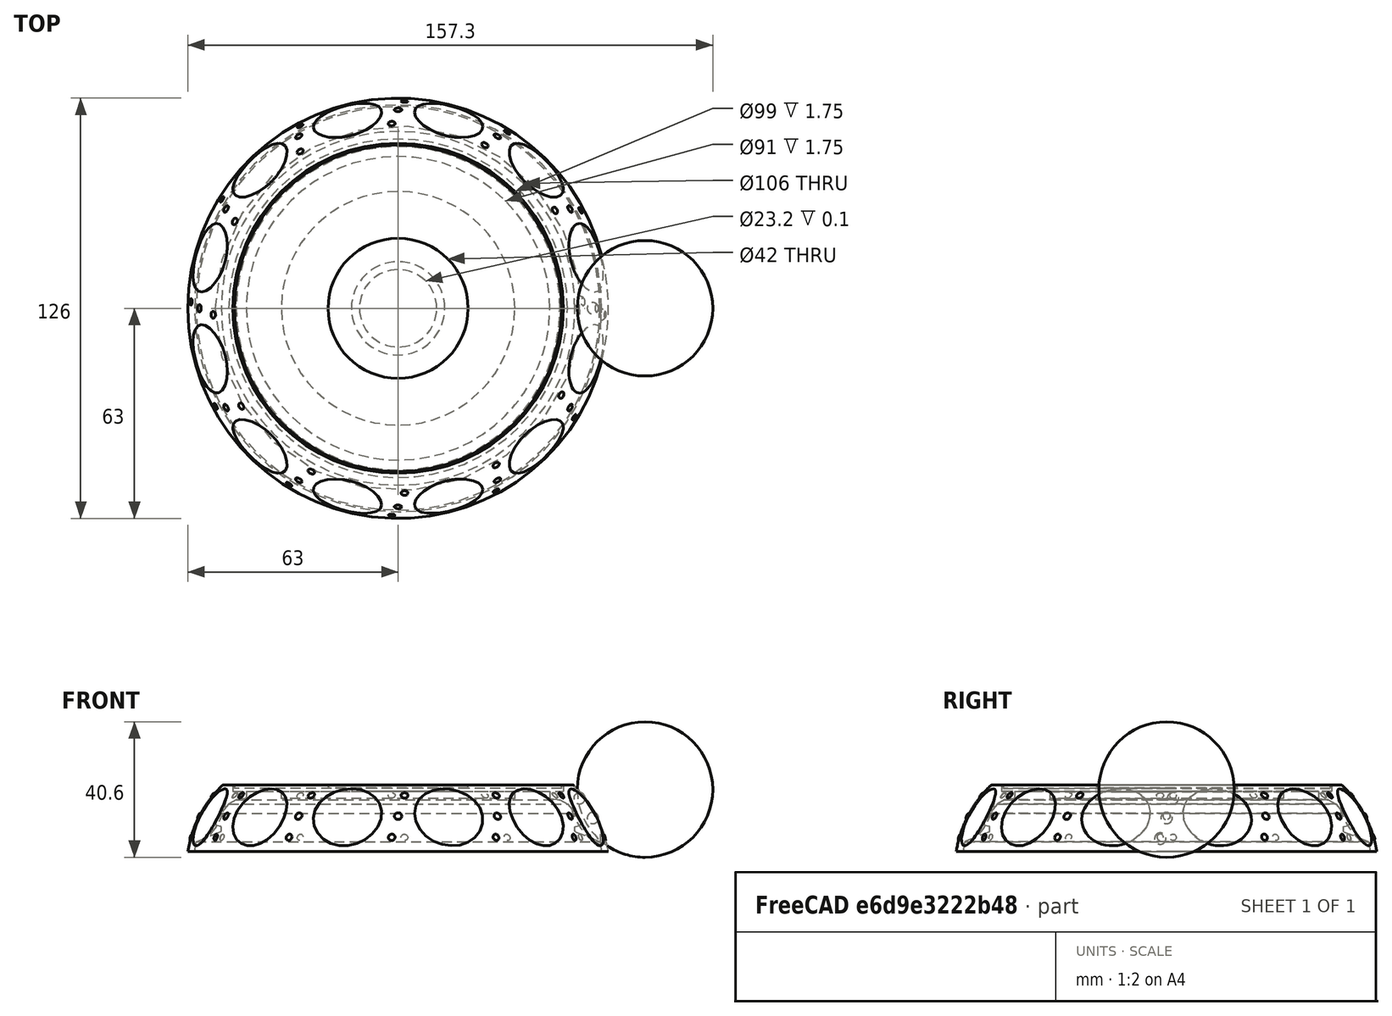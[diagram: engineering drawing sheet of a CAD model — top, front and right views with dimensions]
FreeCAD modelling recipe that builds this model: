
FCSTD DOCUMENT  (FreeCAD 0.20R29177 (Git))
Label: Jog
License: All rights reserved
LicenseURL: http://en.wikipedia.org/wiki/All_rights_reserved
objects: Part::Cylinder×6, Part::Sphere×4, Part::FeaturePython×4, Part::Cut×3, Part::Fuse×3, Sketcher::SketchObject×1, Part::Revolution×1
note: 18 computed .brp shape members not serialized (recipe doc carries the construction recipe); baked Part::Feature solids carry a one-line shape summary decoded from their .brp

FEATURE [Part::Cylinder] Cylinder  label="Поверхность джога"
  Angle = 360
  AttacherType = Attacher::AttachEngine3D
  FirstAngle = 0
  Height = 1
  Placement = pos=(0,0,19) rot=(0,0,1;0rad)
  Radius = 49
  SecondAngle = 0
FEATURE [Sketcher::SketchObject] Sketch
  FullyConstrained = false
  Placement = pos=(0,0,0) rot=(1,0,0;1.5708rad)
  sketch-geometry (20):
    g0: ArcOfCircle CenterX=-28.5028 CenterY=-5.35479 CenterZ=0 NormalX=0 NormalY=0 NormalZ=1 AngleXU=0 Radius=34.9103 StartAngle=2.33675 EndAngle=2.9876
    g1: LineSegment StartX=-61 StartY=0 StartZ=0 EndX=-60.5 EndY=3 EndZ=0
    g2: LineSegment StartX=-54.6347 StartY=8.63919 StartZ=0 EndX=-53 EndY=11.5 EndZ=0
    g3: LineSegment StartX=-63 StartY=0 StartZ=0 EndX=-61 EndY=0 EndZ=0
    g4: LineSegment StartX=-52.2215 StartY=20 StartZ=0 EndX=-49.75 EndY=20 EndZ=0
    g5: LineSegment StartX=-49.5 StartY=19.75 StartZ=0 EndX=-49.5 EndY=18 EndZ=0
    g6: LineSegment StartX=-49.5 StartY=18 StartZ=0 EndX=-45.5 EndY=18 EndZ=0
    g7: LineSegment StartX=-45.7466 StartY=15.9589 StartZ=0 EndX=-48.5 EndY=15.5 EndZ=0
    g8: LineSegment StartX=-48.5 StartY=15.5 StartZ=0 EndX=-50.75 EndY=14.25 EndZ=0
    g9: LineSegment StartX=-50.75 StartY=14.25 StartZ=0 EndX=-53 EndY=11.5 EndZ=0
    g10: LineSegment StartX=-60.5 StartY=3 StartZ=0 EndX=-53.1682 EndY=5.93271 EndZ=0
    g11: LineSegment StartX=-45.5 StartY=18 StartZ=0 EndX=-45.5 EndY=16.25 EndZ=0
    g12: ArcOfCircle CenterX=-52.2215 CenterY=19.3046 CenterZ=0 NormalX=0 NormalY=0 NormalZ=1 AngleXU=0 Radius=0.695441 StartAngle=1.5708 EndAngle=2.33675
    g13: ArcOfCircle CenterX=-45.7951 CenterY=16.25 CenterZ=0 NormalX=0 NormalY=0 NormalZ=1 AngleXU=0 Radius=0.295115 StartAngle=4.87754 EndAngle=6.28319
    g14: ArcOfCircle CenterX=-49.75 CenterY=19.75 CenterZ=0 NormalX=0 NormalY=0 NormalZ=1 AngleXU=0 Radius=0.25 StartAngle=0 EndAngle=1.5708
    g15: LineSegment StartX=-53 StartY=6.18117 StartZ=0 EndX=-53 EndY=7.27425 EndZ=0
    g16: LineSegment StartX=-53.219 StartY=7.55475 StartZ=0 EndX=-54.2858 EndY=7.82145 EndZ=0
    g17: ArcOfCircle CenterX=-54.1505 CenterY=8.3625 CenterZ=0 NormalX=0 NormalY=0 NormalZ=1 AngleXU=0 Radius=0.5577 StartAngle=2.62245 EndAngle=4.46741
    g18: ArcOfCircle CenterX=-53.2891 CenterY=7.27425 CenterZ=0 NormalX=0 NormalY=0 NormalZ=1 AngleXU=0 Radius=0.289138 StartAngle=2e-16 EndAngle=1.32582
    g19: ArcOfCircle CenterX=-53.2676 CenterY=6.18117 CenterZ=0 NormalX=0 NormalY=0 NormalZ=1 AngleXU=0 Radius=0.267599 StartAngle=5.0929 EndAngle=6.28319
  constraints (16):
    c: DistanceX(g0) = -63
    c: DistanceY(g0) = 0
    c: DistanceX(g1) = -61
    c: DistanceY(g1) = 0
    c: Tangent(g0,g12) = -1.5708
    c: Tangent(g4,g12) = 1.5708
    c: Tangent(g11,g13) = 1.5708
    c: Tangent(g7,g13) = 1.5708
    c: Tangent(g4,g14) = 1.5708
    c: Tangent(g5,g14) = 1.5708
    c: Tangent(g2,g17) = 1.5708
    c: Tangent(g16,g17) = 1.5708
    c: Tangent(g16,g18) = -1.5708
    c: Tangent(g15,g18) = -1.5708
    c: Tangent(g10,g19) = -1.5708
    c: Tangent(g15,g19) = -1.5708
FEATURE [Part::Revolution] Revolve
  Angle = 360
  Axis = (0,0,1)
  Base = (0,0,0)
  FaceMakerClass = Part::FaceMakerBullseye
  Solid = true
  Source = -> Sketch
  Symmetric = false
FEATURE [Part::Sphere] Sphere  label="Сфера"
  Angle1 = -90
  Angle2 = 90
  Angle3 = 360
  AttacherType = Attacher::AttachEngine3D
  Placement = pos=(74,0,18.6) rot=(0,0,1;0rad)
  Radius = 20.3
FEATURE [Part::FeaturePython] Array  # Draft array (typed FeaturePython)
  AlwaysSyncPlacement = false
  Angle = 360
  ArrayType = 1
  Axis = (0,0,1)
  Base = -> Sphere
  Center = (0,0,18.6)
  Count = 12
  ExpandArray = false
  Fuse = false
  IntervalAxis = (0,0,0)
  IntervalX = (50,0,0)
  IntervalY = (0,50,0)
  IntervalZ = (0,0,50)
  NumberCircles = 3
  NumberPolar = 12
  NumberX = 2
  NumberY = 2
  NumberZ = 1
  Placement = pos=(0,0,0) rot=(0,0,1;0.261799rad)
  PlacementList = 12 placements: [(74,0,18.6),(64.0859,37,18.6),(37,64.0859,18.6),(0,74,18.6),(-37,64.0859,18.6),(-64.0859,37,18.6),(-74,9.06239e-15,18.6),(-64.0859,-37,18.6),(-37,-64.0859,18.6),(-1.42109e-14,-74,18.6),(37,-64.0859,18.6),(64.0859,-37,18.6)]
  RadialDistance = 50
  ScaleList = (12) [(1,1,1),(1,1,1),(1,1,1),(1,1,1),(1,1,1),(1,1,1),(1,1,1),(1,1,1),(1,1,1),(1,1,1),(1,1,1),(1,1,1)]
  Symmetry = 1
  TangentialDistance = 25
FEATURE [Part::Cut] Cut
  Base = -> Revolve
  Tool = -> Array
FEATURE [Part::Sphere] Sphere001  label="Сфера центральная"
  Angle1 = -90
  Angle2 = 90
  Angle3 = 360
  AttacherType = Attacher::AttachEngine3D
  Placement = pos=(58.38,0,10.05) rot=(0,0,-1;1.5708rad)
  Radius = 1.7
FEATURE [Part::Sphere] Sphere002  label="Сфера нижняя"
  Angle1 = -90
  Angle2 = 90
  Angle3 = 180
  AttacherType = Attacher::AttachEngine3D
  Placement = pos=(60.69,-1.87,3.9) rot=(0,0,-1;1.5708rad)
  Radius = 1.7
FEATURE [Part::Sphere] Sphere003  label="Сфера верхняя"
  Angle1 = -90
  Angle2 = 90
  Angle3 = 360
  AttacherType = Attacher::AttachEngine3D
  Placement = pos=(54.36,1.9,16) rot=(0,0,-1;1.5708rad)
  Radius = 1.7
FEATURE [Part::FeaturePython] Array001  # Draft array (typed FeaturePython)
  AlwaysSyncPlacement = false
  Angle = 360
  ArrayType = 1
  Axis = (0,0,1)
  Base = -> Sphere001
  Center = (0,0,10.05)
  Count = 12
  ExpandArray = false
  Fuse = false
  IntervalAxis = (0,0,0)
  IntervalX = (50,0,0)
  IntervalY = (0,50,0)
  IntervalZ = (0,0,50)
  NumberCircles = 3
  NumberPolar = 12
  NumberX = 2
  NumberY = 2
  NumberZ = 1
  PlacementList = 12 placements: [(58.38,0,10.05),(50.5586,29.19,10.05),(29.19,50.5586,10.05),(0,58.38,10.05),(-29.19,50.5586,10.05),(-50.5586,29.19,10.05),(-58.38,7.14949e-15,10.05),(-50.5586,-29.19,10.05),(-29.19,-50.5586,10.05),(-1.42109e-14,-58.38,10.05),(29.19,-50.5586,10.05),(50.5586,-29.19,10.05)]
  RadialDistance = 50
  ScaleList = (12) [(1,1,1),(1,1,1),(1,1,1),(1,1,1),(1,1,1),(1,1,1),(1,1,1),(1,1,1),(1,1,1),(1,1,1),(1,1,1),(1,1,1)]
  Symmetry = 1
  TangentialDistance = 25
FEATURE [Part::FeaturePython] Array002  # Draft array (typed FeaturePython)
  AlwaysSyncPlacement = false
  Angle = 360
  ArrayType = 1
  Axis = (0,0,1)
  Base = -> Sphere002
  Center = (0,0,3.9)
  Count = 12
  ExpandArray = false
  Fuse = false
  IntervalAxis = (0,0,0)
  IntervalX = (50,0,0)
  IntervalY = (0,50,0)
  IntervalZ = (0,0,50)
  NumberCircles = 3
  NumberPolar = 12
  NumberX = 2
  NumberY = 2
  NumberZ = 1
  PlacementList = 12 placements: [(60.69,-1.87,3.9),(53.4941,28.7255,3.9),(31.9645,51.6241,3.9),(1.87,60.69,3.9),(-28.7255,53.4941,3.9),(-51.6241,31.9645,3.9),(-60.69,1.87,3.9),(-53.4941,-28.7255,3.9),(-31.9645,-51.6241,3.9),(-1.87,-60.69,3.9),(28.7255,-53.4941,3.9),(51.6241,-31.9645,3.9)]
  RadialDistance = 50
  ScaleList = (12) [(1,1,1),(1,1,1),(1,1,1),(1,1,1),(1,1,1),(1,1,1),(1,1,1),(1,1,1),(1,1,1),(1,1,1),(1,1,1),(1,1,1)]
  Symmetry = 1
  TangentialDistance = 25
FEATURE [Part::FeaturePython] Array003  # Draft array (typed FeaturePython)
  AlwaysSyncPlacement = false
  Angle = 360
  ArrayType = 1
  Axis = (0,0,1)
  Base = -> Sphere003
  Center = (0,0,16)
  Count = 12
  ExpandArray = false
  Fuse = false
  IntervalAxis = (0,0,0)
  IntervalX = (50,0,0)
  IntervalY = (0,50,0)
  IntervalZ = (0,0,50)
  NumberCircles = 3
  NumberPolar = 12
  NumberX = 2
  NumberY = 2
  NumberZ = 1
  PlacementList = 12 placements: [(54.36,1.9,16),(46.1271,28.8254,16),(25.5346,48.0271,16),(-1.9,54.36,16),(-28.8254,46.1271,16),(-48.0271,25.5346,16),(-54.36,-1.9,16),(-46.1271,-28.8254,16),(-25.5346,-48.0271,16),(1.9,-54.36,16),(28.8254,-46.1271,16),(48.0271,-25.5346,16)]
  RadialDistance = 50
  ScaleList = (12) [(1,1,1),(1,1,1),(1,1,1),(1,1,1),(1,1,1),(1,1,1),(1,1,1),(1,1,1),(1,1,1),(1,1,1),(1,1,1),(1,1,1)]
  Symmetry = 1
  TangentialDistance = 25
FEATURE [Part::Cylinder] Cylinder001  label="Цилиндр"
  Angle = 360
  AttacherType = Attacher::AttachEngine3D
  FirstAngle = 0
  Height = 0.1
  Placement = pos=(0,0,25) rot=(0,0,1;0rad)
  Radius = 14
  SecondAngle = 0
FEATURE [Part::Cylinder] Cylinder002  label="Цилиндр001"
  Angle = 360
  AttacherType = Attacher::AttachEngine3D
  FirstAngle = 0
  Height = 0.1
  Placement = pos=(0,0,25) rot=(0,0,1;0rad)
  Radius = 11.6
  SecondAngle = 0
FEATURE [Part::Cut] Cut001
  Base = -> Cylinder001
  Placement = pos=(0,0,-7.1) rot=(0,0,1;0rad)
  Tool = -> Cylinder002
FEATURE [Part::Cylinder] Cylinder003  label="Поверхность джога001"
  Angle = 360
  AttacherType = Attacher::AttachEngine3D
  FirstAngle = 0
  Height = 1
  Placement = pos=(0,0,19) rot=(0,0,1;0rad)
  Radius = 21
  SecondAngle = 0
FEATURE [Part::Cut] Cut002
  Base = -> Cylinder
  Tool = -> Cylinder003
FEATURE [Part::Cylinder] Cylinder004  label="LCD"
  Angle = 360
  AttacherType = Attacher::AttachEngine3D
  FirstAngle = 0
  Height = 2
  Placement = pos=(0,0,15.9) rot=(0,0,1;0rad)
  Radius = 35
  SecondAngle = 0
FEATURE [Part::Fuse] Fusion
  Base = -> Cut
  Tool = -> Array001
FEATURE [Part::Fuse] Fusion001
  Base = -> Fusion
  Tool = -> Array002
FEATURE [Part::Fuse] Fusion002
  Base = -> Fusion001
  Tool = -> Array003
FEATURE [Part::Cylinder] Cylinder005  label="glass"
  Angle = 360
  AttacherType = Attacher::AttachEngine3D
  FirstAngle = 0
  Height = 0.96
  Placement = pos=(0,0,19.03) rot=(0,0,1;0rad)
  Radius = 21
  SecondAngle = 0
